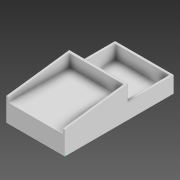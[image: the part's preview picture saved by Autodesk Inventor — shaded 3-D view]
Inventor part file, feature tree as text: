
AUTODESK INVENTOR PART (.ipt)
format: ipt  version: 2020.2 (Build 242310000, 310)  size: 149,504 bytes
history: native  units: mm
features: extrude x5, sketch x5
ambient origin geometry x8: Origin, YZ Plane, XZ Plane, XY Plane, X Axis, Y Axis, Z Axis, Center Point
bodies: Solid1 (feature_tree)
feature tree (10):
  extrude  "Extrusion1"  Depth=156.0mm
  extrude  "Extrusion2"  Depth=3.0mm
  extrude  "Extrusion3"  Depth=150.0mm
  sketch  "Sketch5"  dims[d15=3.0mm d16=33.5mm]
  sketch  "Sketch6"  dims[d17=20.0mm d18=0.0mm d19=90.225mm d20=3.0mm d21=70.5mm d22=0.0mm d27=3.0mm d28=78.0mm d29=7.0mm d34=10.0mm d35=0.0mm d40=87.25mm d41=0.0mm d32=0.5mm d33=0.872665mm d42=0.5mm d43=0.872665mm d44=0.5mm d45=0.872665mm]
  extrude  "Extrusion7"  Depth=3.0mm
  extrude  "Extrusion10"  Depth=90.225mm
  sketch  "Sketch1"  dims[d0=84.0mm d1=156.0mm]
  sketch  "Sketch2"  dims[d10=3.0mm d11=0.0mm d12=42.0mm]
  sketch  "Sketch3"  dims[d13=78.0mm d14=150.0mm]
